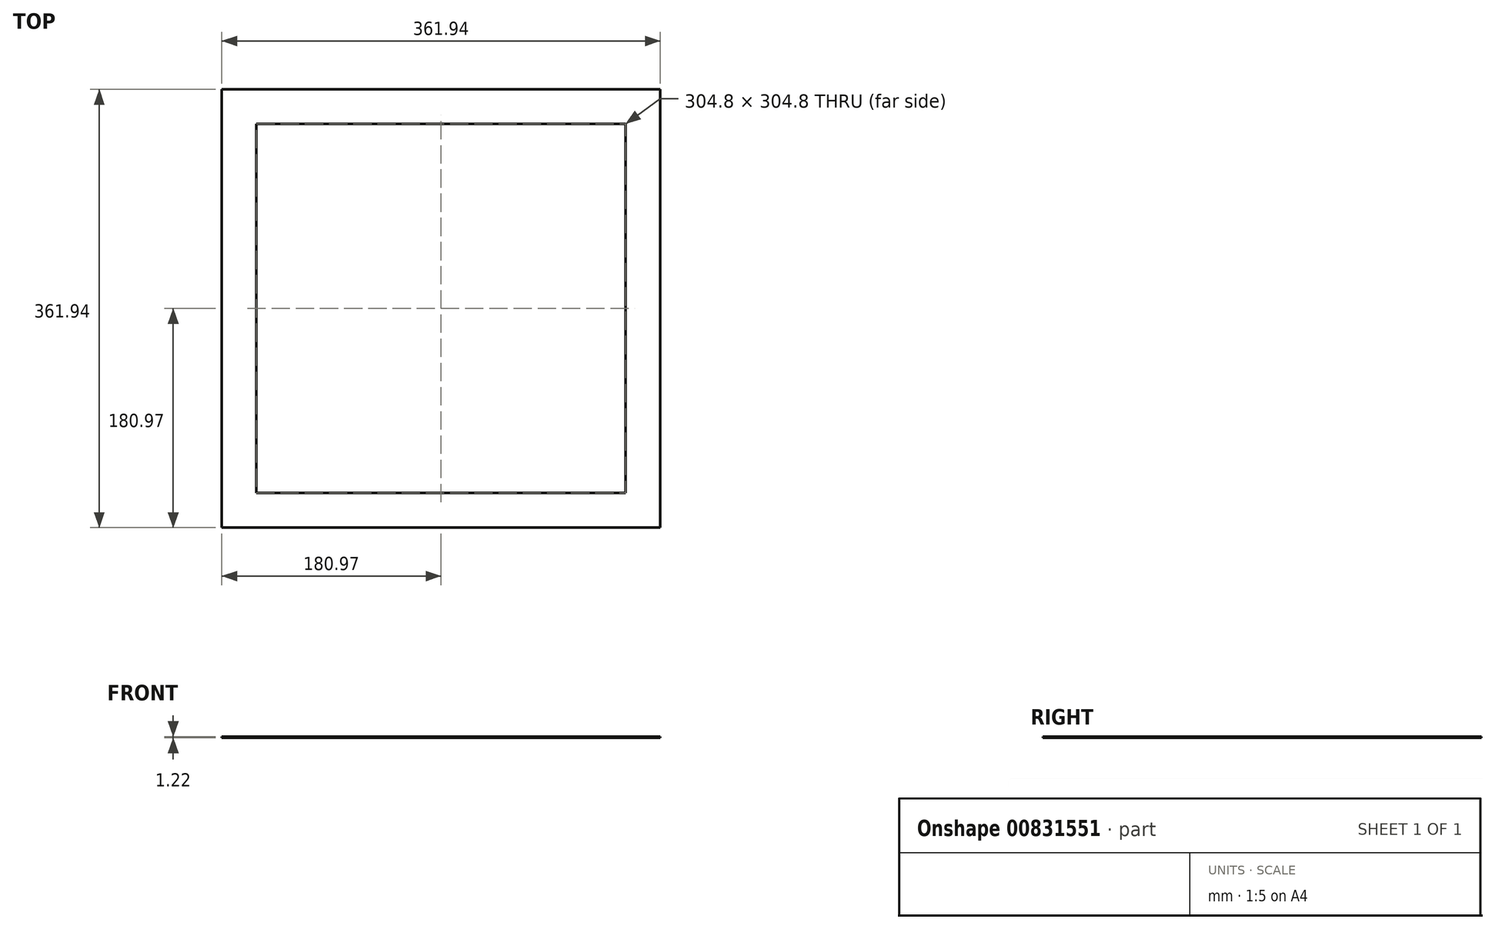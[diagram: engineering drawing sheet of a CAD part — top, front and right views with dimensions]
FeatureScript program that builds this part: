
annotation { "Feature Type Name" : "Feature", "Feature Type Description" : "" }
export const myFeature = defineFeature(function(context is Context, id is Id, definition is map)
    precondition{}
    {
        {
            var Q0;
            Q0=qCreatedBy(makeId("Top.planeOp"),FACE);
            var sketch = newSketch(context, id + "F0", { "sketchPlane" : qUnion([Q0])});
            skLineSegment(sketch, "E0.bottom", {"start": v(-180.97, 180.98) * mm, "end": v(180.97, 180.98) * mm});
            skLineSegment(sketch, "E0.top", {"start": v(-180.97, -180.97) * mm, "end": v(180.98, -180.97) * mm});
            skLineSegment(sketch, "E0.left", {"start": v(-180.97, 180.98) * mm, "end": v(-180.97, -180.97) * mm});
            skLineSegment(sketch, "E0.right", {"start": v(180.97, 180.98) * mm, "end": v(180.97, -180.97) * mm});
            skLineSegment(sketch, "E1.bottom", {"start": v(-152.4, 152.4) * mm, "end": v(152.4, 152.4) * mm});
            skLineSegment(sketch, "E1.top", {"start": v(-152.4, -152.4) * mm, "end": v(152.4, -152.4) * mm});
            skLineSegment(sketch, "E1.left", {"start": v(-152.4, 152.4) * mm, "end": v(-152.4, -152.4) * mm});
            skLineSegment(sketch, "E1.right", {"start": v(152.4, 152.4) * mm, "end": v(152.4, -152.4) * mm});
            skLineSegment(sketch, "E2", {"start": v(0, 0) * mm, "end": v(0, 152.4) * mm, "construction": true});
            skLineSegment(sketch, "E3", {"start": v(0, 0) * mm, "end": v(-152.4, 0) * mm, "construction": true});
            skLineSegment(sketch, "E4", {"start": v(0, 152.4) * mm, "end": v(0, 180.98) * mm, "construction": true});
            skLineSegment(sketch, "E5", {"start": v(-152.4, 0) * mm, "end": v(-180.97, 0) * mm, "construction": true});
            skSolve(sketch);
        }
        {
            var Q0;
            Q0=makeQuery(id+"F0.imprint","IMPRINT",FACE,{"disambiguationData":[TD([[makeQuery(id+"F0.imprint","IMPRINT",EDGE,{"derivedFrom":sQuery(id+"F0.wireOp",EDGE,"E0.bottom")}),-1.0]])]});
            extrude(context, id + "F1", {"entities" : qUnion([Q0]), "depth" : 1.22 * mm, "offsetDistance" : 25.4 * mm});
        }
    });
